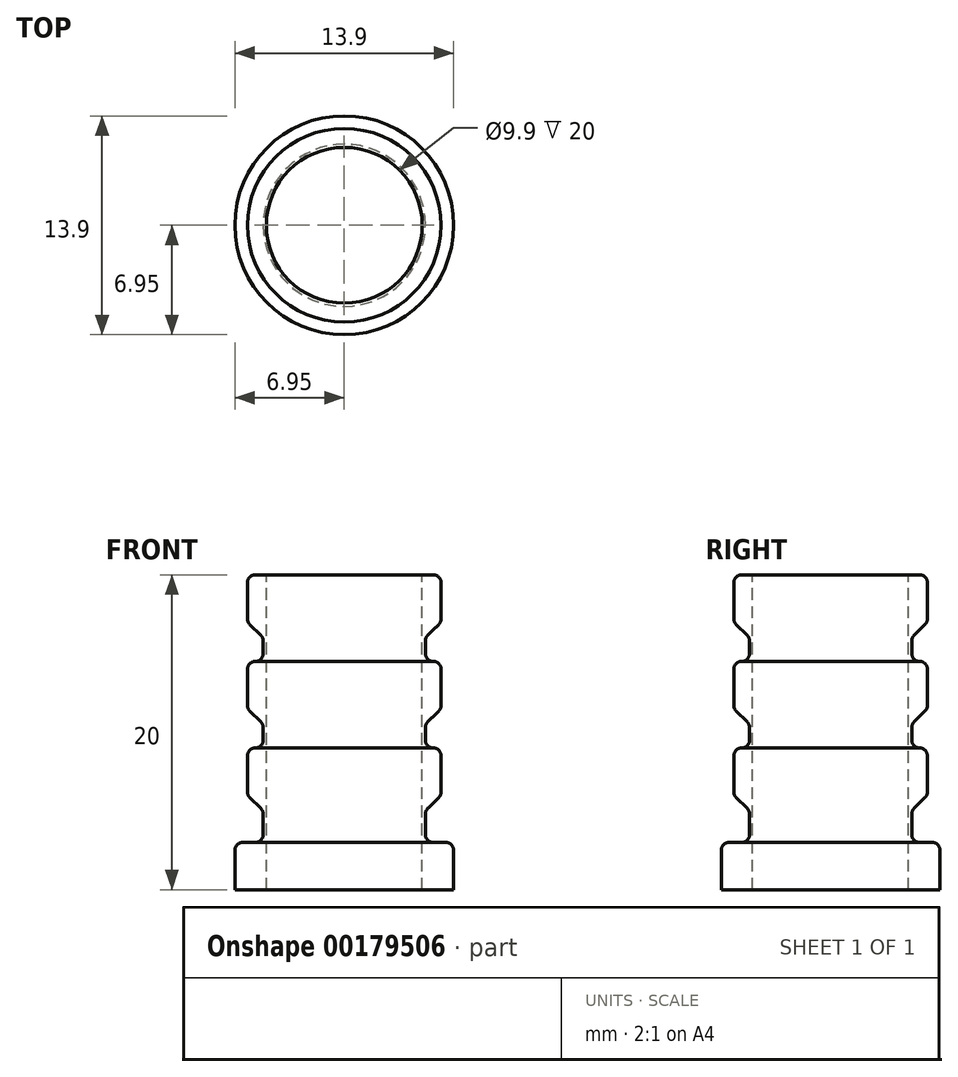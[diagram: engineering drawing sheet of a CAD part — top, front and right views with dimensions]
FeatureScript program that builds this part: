
annotation { "Feature Type Name" : "Feature", "Feature Type Description" : "" }
export const myFeature = defineFeature(function(context is Context, id is Id, definition is map)
    precondition{}
    {
        {
            var Q0;
            Q0=qCreatedBy(makeId("Front.planeOp"),FACE);
            var sketch = newSketch(context, id + "F0", { "sketchPlane" : qUnion([Q0])});
            skLineSegment(sketch, "E0", {"start": v(0, -9.29) * mm, "end": v(2, -9.29) * mm});
            skLineSegment(sketch, "E1", {"start": v(2, -9.29) * mm, "end": v(2, -6.79) * mm});
            skLineSegment(sketch, "E2", {"start": v(1.5, -6.29) * mm, "end": v(0.7, -6.29) * mm});
            skLineSegment(sketch, "E3", {"start": v(1.2, -3.08) * mm, "end": v(1.2, -0.79) * mm});
            skLineSegment(sketch, "E4", {"start": v(0.7, -0.29) * mm, "end": v(0.7, -0.29) * mm});
            skLineSegment(sketch, "E5", {"start": v(1.2, 2.42) * mm, "end": v(1.2, 4.71) * mm});
            skLineSegment(sketch, "E6", {"start": v(0.7, 5.21) * mm, "end": v(0.7, 5.21) * mm});
            skLineSegment(sketch, "E7", {"start": v(1.2, 7.92) * mm, "end": v(1.2, 10.21) * mm});
            skLineSegment(sketch, "E8", {"start": v(0.7, 10.71) * mm, "end": v(0, 10.71) * mm});
            skLineSegment(sketch, "E9", {"start": v(-4.95, 13.6) * mm, "end": v(-4.95, -29.13) * mm, "construction": true});
            skLineSegment(sketch, "E10", {"start": v(0, 10.71) * mm, "end": v(0, -9.29) * mm});
            skLineSegment(sketch, "E11", {"start": v(0.2, 5.71) * mm, "end": v(0.2, 6.5) * mm});
            skLineSegment(sketch, "E12", {"start": v(0.35, 6.86) * mm, "end": v(1.05, 7.56) * mm});
            skLineSegment(sketch, "E13", {"start": v(0.2, 0.21) * mm, "end": v(0.2, 1) * mm});
            skLineSegment(sketch, "E14", {"start": v(0.35, 1.36) * mm, "end": v(1.05, 2.06) * mm});
            skLineSegment(sketch, "E15", {"start": v(0.2, -5.79) * mm, "end": v(0.2, -4.5) * mm});
            skLineSegment(sketch, "E16", {"start": v(0.35, -4.14) * mm, "end": v(1.05, -3.44) * mm});
            skPoint(sketch, "E17.endSnap0", {"position": v(1.2, 3.71) * mm});
            skPoint(sketch, "E18.visualSharp", {"position": v(0.2, -6.29) * mm});
            skArc(sketch, "E18.filletArc", {"start": v(0.2, -5.79) * mm, "mid": v(0.35, -6.14) * mm, "end": v(0.7, -6.29) * mm});
            skPoint(sketch, "E19.visualSharp", {"position": v(0.2, -4.29) * mm});
            skArc(sketch, "E19.filletArc", {"start": v(0.35, -4.14) * mm, "mid": v(0.24, -4.3) * mm, "end": v(0.2, -4.5) * mm});
            skPoint(sketch, "E20.visualSharp", {"position": v(1.2, -3.29) * mm});
            skArc(sketch, "E20.filletArc", {"start": v(1.05, -3.44) * mm, "mid": v(1.16, -3.27) * mm, "end": v(1.2, -3.08) * mm});
            skPoint(sketch, "E21.visualSharp", {"position": v(1.2, -0.29) * mm});
            skArc(sketch, "E21.filletArc", {"start": v(1.2, -0.79) * mm, "mid": v(1.05, -0.44) * mm, "end": v(0.7, -0.29) * mm});
            skPoint(sketch, "E22.visualSharp", {"position": v(0.2, -0.29) * mm});
            skArc(sketch, "E22.filletArc", {"start": v(0.2, 0.21) * mm, "mid": v(0.35, -0.14) * mm, "end": v(0.7, -0.29) * mm});
            skPoint(sketch, "E23.visualSharp", {"position": v(1.2, 2.21) * mm});
            skArc(sketch, "E23.filletArc", {"start": v(1.05, 2.06) * mm, "mid": v(1.16, 2.23) * mm, "end": v(1.2, 2.42) * mm});
            skPoint(sketch, "E24.visualSharp", {"position": v(1.2, 5.21) * mm});
            skArc(sketch, "E24.filletArc", {"start": v(1.2, 4.71) * mm, "mid": v(1.05, 5.06) * mm, "end": v(0.7, 5.21) * mm});
            skPoint(sketch, "E25.visualSharp", {"position": v(0.2, 6.71) * mm});
            skArc(sketch, "E25.filletArc", {"start": v(0.35, 6.86) * mm, "mid": v(0.24, 6.7) * mm, "end": v(0.2, 6.5) * mm});
            skPoint(sketch, "E26.visualSharp", {"position": v(0.2, 5.21) * mm});
            skArc(sketch, "E26.filletArc", {"start": v(0.2, 5.71) * mm, "mid": v(0.35, 5.36) * mm, "end": v(0.7, 5.21) * mm});
            skPoint(sketch, "E27.visualSharp", {"position": v(0.2, 1.21) * mm});
            skArc(sketch, "E27.filletArc", {"start": v(0.35, 1.36) * mm, "mid": v(0.24, 1.2) * mm, "end": v(0.2, 1) * mm});
            skPoint(sketch, "E28.visualSharp", {"position": v(1.2, 7.71) * mm});
            skArc(sketch, "E28.filletArc", {"start": v(1.05, 7.56) * mm, "mid": v(1.16, 7.73) * mm, "end": v(1.2, 7.92) * mm});
            skPoint(sketch, "E29.visualSharp", {"position": v(1.2, 10.71) * mm});
            skArc(sketch, "E29.filletArc", {"start": v(1.2, 10.21) * mm, "mid": v(1.05, 10.56) * mm, "end": v(0.7, 10.71) * mm});
            skPoint(sketch, "E30.visualSharp", {"position": v(2, -6.29) * mm});
            skArc(sketch, "E30.filletArc", {"start": v(2, -6.79) * mm, "mid": v(1.85, -6.44) * mm, "end": v(1.5, -6.29) * mm});
            skSolve(sketch);
        }
        {
            var Q0;
            Q0 = qSketchRegion(id + "F0", true);
            var Q1;
            Q1=sQuery(id+"F0.wireOp",EDGE,"E9");
            revolve(context, id + "F1", {"entities" : qUnion([Q0]), "axis" : qUnion([Q1]), "revolveType" : RevolveType.FULL});
        }
    });
